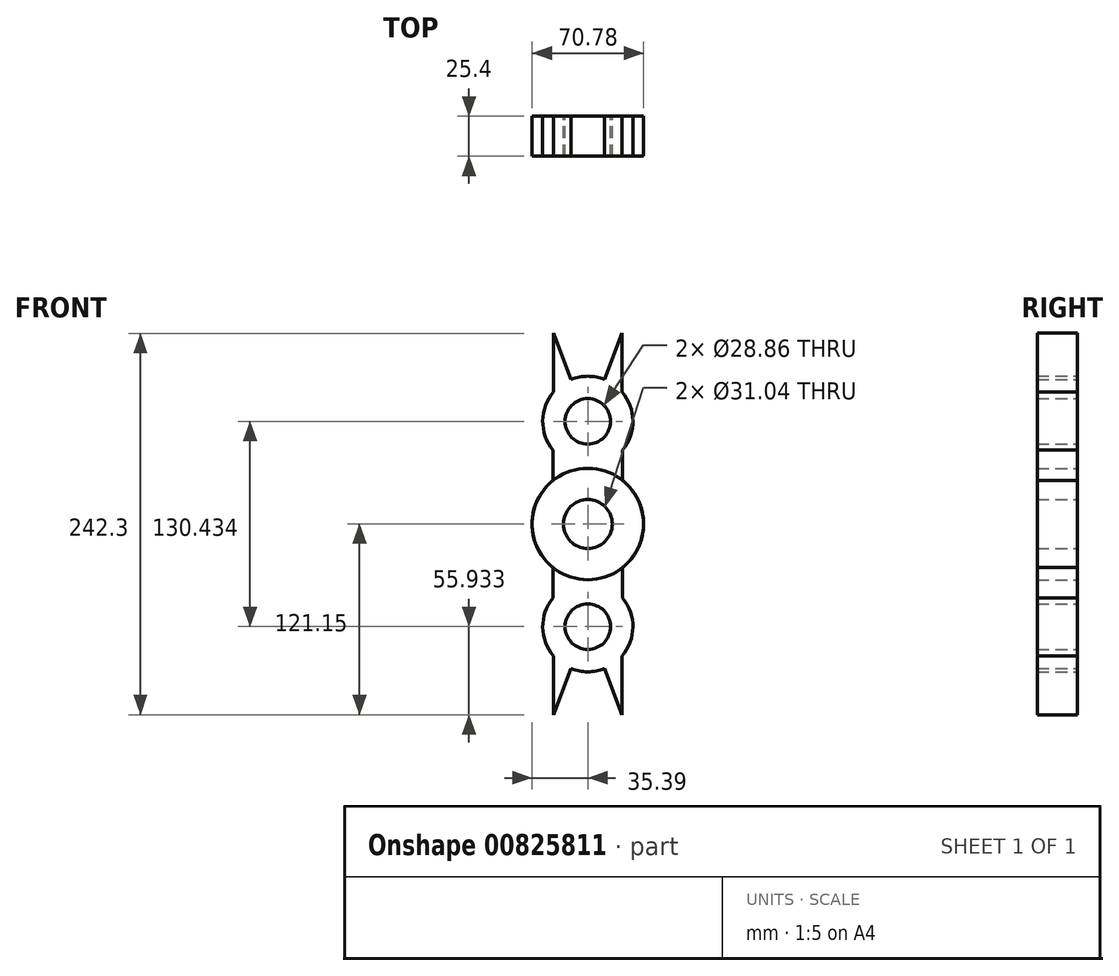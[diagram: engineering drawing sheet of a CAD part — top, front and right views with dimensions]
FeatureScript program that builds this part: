
annotation { "Feature Type Name" : "Feature", "Feature Type Description" : "" }
export const myFeature = defineFeature(function(context is Context, id is Id, definition is map)
    precondition{}
    {
        {
            var Q0;
            Q0=qCreatedBy(makeId("Front.planeOp"),FACE);
            var sketch = newSketch(context, id + "F0", { "sketchPlane" : qUnion([Q0])});
            skArc(sketch, "E0", {"start": v(22.1, 47) * mm, "mid": v(23.14, 82.1) * mm, "end": v(-10.6, 91.83) * mm});
            skLineSegment(sketch, "E1.top", {"start": v(-22.1, 47) * mm, "end": v(-22.1, 47) * mm});
            skLineSegment(sketch, "E1.left", {"start": v(-22.1, 27.64) * mm, "end": v(-22.1, 47) * mm});
            skLineSegment(sketch, "E1.right", {"start": v(22.1, 27.64) * mm, "end": v(22.1, 47) * mm});
            skCircle(sketch, "E2", {"center": v(0, 65.22) * mm, "radius": 14.43 * mm});
            skLineSegment(sketch, "E3", {"start": v(-21.71, 83.9) * mm, "end": v(-21.71, 121.15) * mm});
            skLineSegment(sketch, "E4", {"start": v(-21.71, 121.15) * mm, "end": v(-10.6, 91.83) * mm});
            skArc(sketch, "E5.trimOffspring", {"start": v(-21.71, 83.9) * mm, "mid": v(-28.64, 65.52) * mm, "end": v(-22.1, 47) * mm});
            skLineSegment(sketch, "E6.MirrorCS", {"start": v(21.71, 83.9) * mm, "end": v(21.71, 121.15) * mm});
            skLineSegment(sketch, "E7.MirrorCS", {"start": v(21.71, 121.15) * mm, "end": v(10.6, 91.83) * mm});
            skArc(sketch, "E8", {"start": v(-22.1, 27.64) * mm, "mid": v(0, -35.39) * mm, "end": v(22.1, 27.64) * mm});
            skPoint(sketch, "E1.bottom.start.orphan", {"position": v(-22.1, 0) * mm});
            skCircle(sketch, "E9", {"center": v(0, 0) * mm, "radius": 15.52 * mm});
            skSolve(sketch);
        }
        {
            var Q0;
            Q0 = qSketchRegion(id + "F0", true);
            extrude(context, id + "F1", {"entities" : qUnion([Q0]), "depth" : 25.4 * mm, "offsetDistance" : 25.4 * mm});
        }
        {
            var Q0;
            Q0=qCreatedBy(makeId("Top.planeOp"),FACE);
            var sketch = newSketch(context, id + "F2", { "sketchPlane" : qUnion([Q0])});
            skLineSegment(sketch, "E10", {"start": v(0, 0) * mm, "end": v(0, -64.36) * mm, "construction": true});
            skSolve(sketch);
        }
        {
            var Q0;
            Q0=makeQuery(id+"F1.opExtrude","SWEPT_BODY",BODY,{"disambiguationData":[OSD([sQuery(id+"F0.wireOp",EDGE,"E0"),sQuery(id+"F0.wireOp",EDGE,"E1.left"),sQuery(id+"F0.wireOp",EDGE,"E1.right"),sQuery(id+"F0.wireOp",EDGE,"E2"),sQuery(id+"F0.wireOp",EDGE,"E3"),sQuery(id+"F0.wireOp",EDGE,"E4"),sQuery(id+"F0.wireOp",EDGE,"E5.trimOffspring"),sQuery(id+"F0.wireOp",EDGE,"E6.MirrorCS"),sQuery(id+"F0.wireOp",EDGE,"E7.MirrorCS"),sQuery(id+"F0.wireOp",EDGE,"E8"),sQuery(id+"F0.wireOp",EDGE,"E9")])]});
            var Q1;
            Q1=sQuery(id+"F2.wireOp",EDGE,"E10");
            circularPattern(context, id + "F3", {"entities" : qUnion([Q0]), "axis" : qUnion([Q1]), "angle" : 180 * degree, "instanceCount" : 2, "equalSpace" : true});
        }
    });
